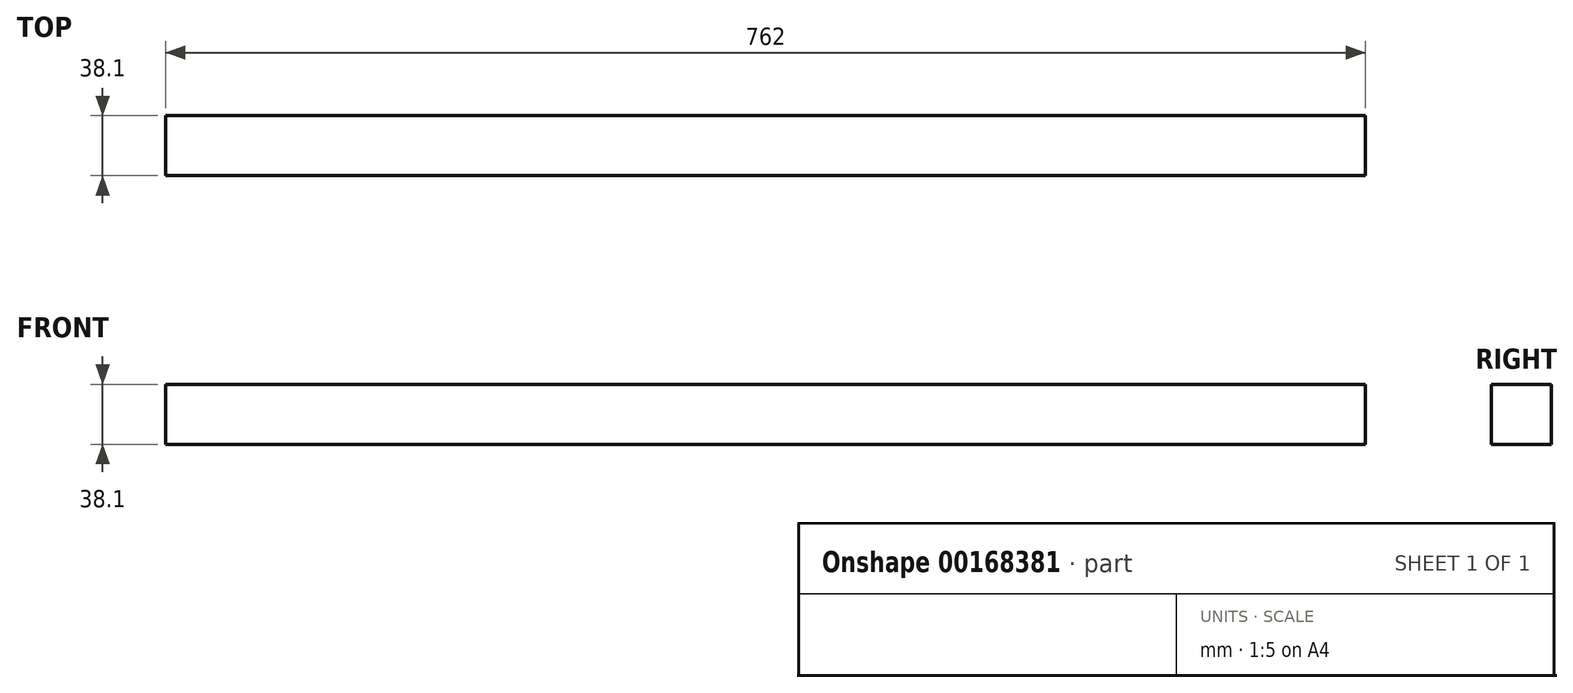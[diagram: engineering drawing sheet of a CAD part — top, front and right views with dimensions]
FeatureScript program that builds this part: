
annotation { "Feature Type Name" : "Feature", "Feature Type Description" : "" }
export const myFeature = defineFeature(function(context is Context, id is Id, definition is map)
    precondition{}
    {
        {
            var Q0;
            Q0=qCreatedBy(makeId("Top.planeOp"),FACE);
            var sketch = newSketch(context, id + "F0", { "sketchPlane" : qUnion([Q0])});
            skLineSegment(sketch, "E0.bottom", {"start": v(-381, 19.05) * mm, "end": v(381, 19.05) * mm});
            skLineSegment(sketch, "E0.top", {"start": v(-381, -19.05) * mm, "end": v(381, -19.05) * mm});
            skLineSegment(sketch, "E0.left", {"start": v(-381, 19.05) * mm, "end": v(-381, -19.05) * mm});
            skLineSegment(sketch, "E0.right", {"start": v(381, 19.05) * mm, "end": v(381, -19.05) * mm});
            skPoint(sketch, "E0.middle", {"position": v(0, 0) * mm});
            skSolve(sketch);
        }
        {
            var Q0;
            Q0=makeQuery(id+"F0.imprint","IMPRINT",FACE,{"disambiguationData":[TD([[makeQuery(id+"F0.imprint","IMPRINT",EDGE,{"derivedFrom":sQuery(id+"F0.wireOp",EDGE,"E0.bottom")}),-1.0]])]});
            extrude(context, id + "F1", {"entities" : qUnion([Q0]), "depth" : 38.1 * mm});
        }
    });
